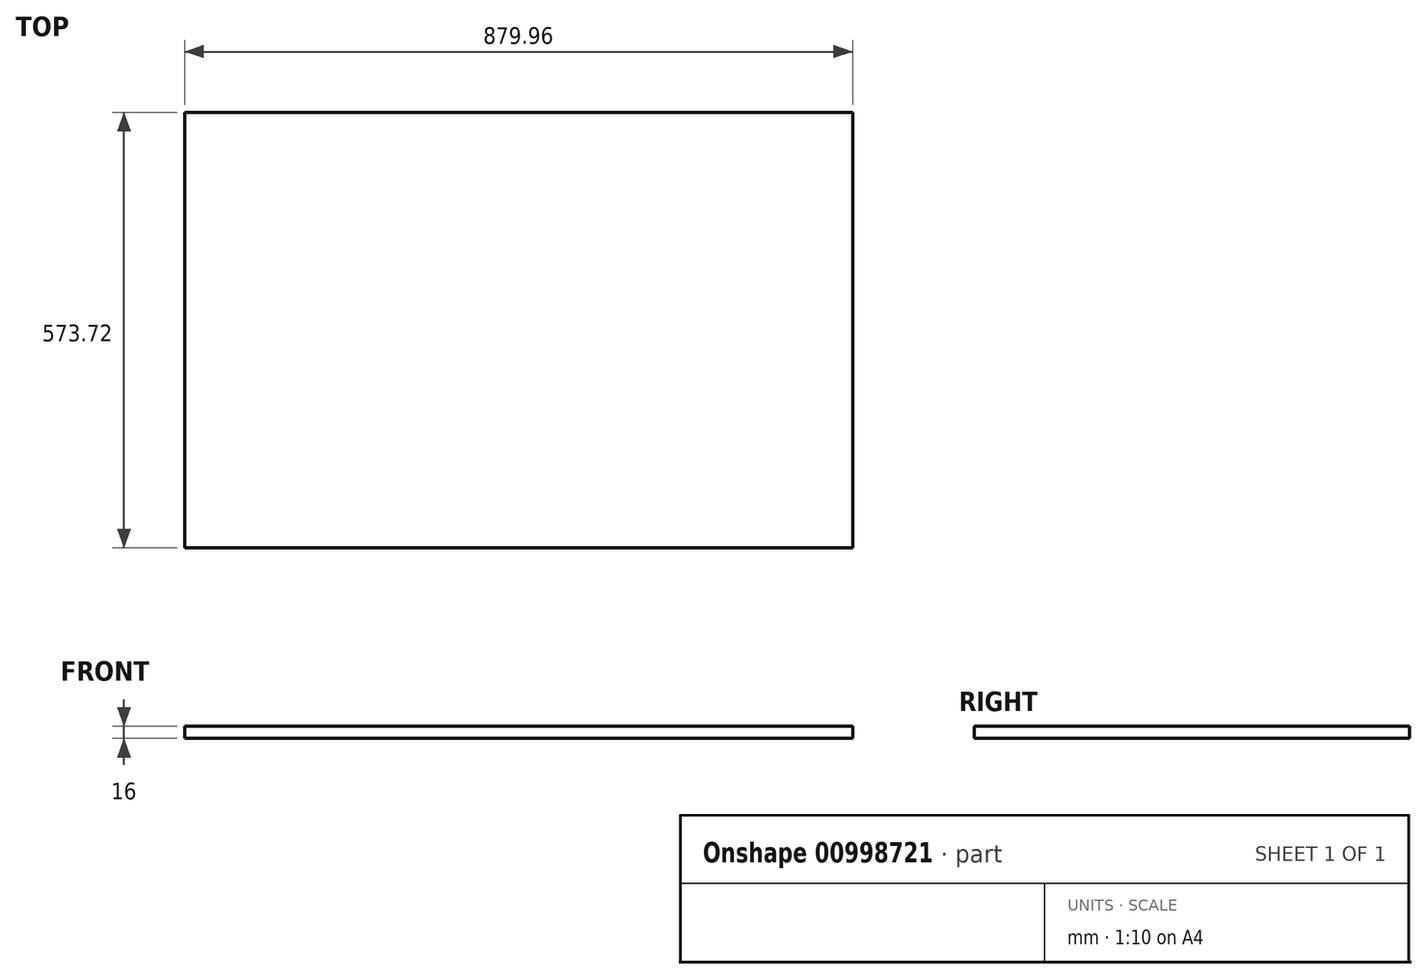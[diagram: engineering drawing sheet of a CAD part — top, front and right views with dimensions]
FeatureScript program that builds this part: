
annotation { "Feature Type Name" : "Feature", "Feature Type Description" : "" }
export const myFeature = defineFeature(function(context is Context, id is Id, definition is map)
    precondition{}
    {
        {
            var Q0;
            Q0=qCreatedBy(makeId("Top.planeOp"),FACE);
            var sketch = newSketch(context, id + "F0", { "sketchPlane" : qUnion([Q0])});
            skLineSegment(sketch, "E0.bottom", {"start": v(-50, -30) * mm, "end": v(950, -30) * mm});
            skLineSegment(sketch, "E0.top", {"start": v(-50, 570) * mm, "end": v(950, 570) * mm});
            skLineSegment(sketch, "E0.left", {"start": v(-50, -30) * mm, "end": v(-50, 570) * mm});
            skLineSegment(sketch, "E0.right", {"start": v(950, -30) * mm, "end": v(950, 570) * mm});
            skLineSegment(sketch, "E1", {"start": v(950, 570) * mm, "end": v(-50, 570) * mm});
            skSolve(sketch);
        }
        {
            var Q0;
            Q0=makeQuery(id+"F0.imprint","IMPRINT",FACE,{"disambiguationData":[TD([[makeQuery(id+"F0.imprint","IMPRINT",EDGE,{"derivedFrom":sQuery(id+"F0.wireOp",EDGE,"E0.left")}),-1.0]])]});
            extrude(context, id + "F1", {"entities" : qUnion([Q0]), "depth" : 380 * mm, "offsetDistance" : 25 * mm});
        }
        {
            var Q0;
            Q0=makeQuery(id+"F1.opExtrude","CAP_EDGE",EDGE,{"disambiguationData":[OSD([sQuery(id+"F0.wireOp",EDGE,"E0.left")])],"isStart":false});
            var Q1;
            Q1=makeQuery(id+"F1.opExtrude","CAP_EDGE",EDGE,{"disambiguationData":[OSD([sQuery(id+"F0.wireOp",EDGE,"E0.right")])],"isStart":false});
            fillet(context, id + "F2", {"entities" : qUnion([Q0, Q1]), "radius" : 60 * mm, "tangentPropagation" : true, "allowEdgeOverflow" : false});
        }
        {
            var Q0;
            Q0=makeQuery(id+"F1.opExtrude","CAP_EDGE",EDGE,{"disambiguationData":[OSD([sQuery(id+"F0.wireOp",EDGE,"E0.bottom")])],"isStart":true});
            var Q1;
            Q1=makeQuery(id+"F1.opExtrude","CAP_EDGE",EDGE,{"disambiguationData":[OSD([sQuery(id+"F0.wireOp",EDGE,"E1")])],"isStart":true});
            fillet(context, id + "F3", {"entities" : qUnion([Q0, Q1]), "radius" : 60 * mm, "tangentPropagation" : true, "allowEdgeOverflow" : false});
        }
        {
            var Q0;
            Q0=makeQuery(id+"F1.opExtrude","CAP_FACE",FACE,{"disambiguationData":[OSD([sQuery(id+"F0.wireOp",EDGE,"E0.left"),sQuery(id+"F0.wireOp",EDGE,"E0.right"),sQuery(id+"F0.wireOp",EDGE,"E0.bottom"),sQuery(id+"F0.wireOp",EDGE,"E1")])],"isStart":false});
            cPlane(context, id + "F4", {"entities" : qUnion([Q0]), "cplaneType" : CPlaneType.OFFSET, "offset" : 0 * mm, "width" : 150 * mm, "height" : 150 * mm});
        }
        {
            var Q0;
            Q0=makeQuery(id+"F1.opExtrude","CAP_EDGE",EDGE,{"disambiguationData":[OSD([sQuery(id+"F0.wireOp",EDGE,"E0.bottom")])],"isStart":false});
            cPoint(context, id + "F5", {"entities" : qUnion([Q0]), "parameter" : 0.5});
        }
        {
            var Q0;
            Q0 = qCreatedBy(id + "F5" ,VERTEX);
            var Q1;
            Q1=makeQuery(id+"F1.opExtrude","CAP_EDGE",EDGE,{"disambiguationData":[OSD([sQuery(id+"F0.wireOp",EDGE,"E0.bottom")])],"isStart":false});
            cPlane(context, id + "F6", {"entities" : qUnion([Q0, Q1]), "cplaneType" : CPlaneType.LINE_POINT, "offset" : 25 * mm, "width" : 150 * mm, "height" : 150 * mm});
        }
        {
            var Q0;
            Q0=qCreatedBy(id+"F6.planeOp",FACE);
            var sketch = newSketch(context, id + "F7", { "sketchPlane" : qUnion([Q0])});
            skCircle(sketch, "E2", {"center": v(-31.89, 381.57) * mm, "radius": 15 * mm});
            skSolve(sketch);
        }
        {
            var Q0;
            Q0=makeQuery(id+"F1.opExtrude","SWEPT_FACE",FACE,{"disambiguationData":[OSD([sQuery(id+"F0.wireOp",EDGE,"E0.bottom")])]});
            extrude(context, id + "F8", {"entities" : qUnion([Q0]), "operationType" : NewBodyOperationType.REMOVE, "endBound" : BoundingType.THROUGH_ALL, "oppositeDirection" : true, "depth" : 25 * mm, "offsetDistance" : 25 * mm});
        }
        {
            var Q0;
            Q0=makeQuery(id+"F1.opExtrude","SWEPT_FACE",FACE,{"disambiguationData":[OSD([sQuery(id+"F0.wireOp",EDGE,"E0.right")])]});
            extrude(context, id + "F9", {"entities" : qUnion([Q0]), "operationType" : NewBodyOperationType.REMOVE, "endBound" : BoundingType.THROUGH_ALL, "oppositeDirection" : true, "depth" : 25 * mm, "offsetDistance" : 25 * mm});
        }
        {
            var Q0;
            Q0=qCreatedBy(id+"F4.planeOp",FACE);
            var sketch = newSketch(context, id + "F10", { "sketchPlane" : qUnion([Q0])});
            skLineSegment(sketch, "E3.bottom", {"start": v(889.96, 556.82) * mm, "end": v(10, 556.82) * mm});
            skLineSegment(sketch, "E3.top", {"start": v(889.96, -16.9) * mm, "end": v(10, -16.9) * mm});
            skLineSegment(sketch, "E3.left", {"start": v(889.96, 556.82) * mm, "end": v(889.96, -16.9) * mm});
            skLineSegment(sketch, "E3.right", {"start": v(10, 556.82) * mm, "end": v(10, -16.9) * mm});
            skSolve(sketch);
        }
        {
            var Q0;
            Q0=makeQuery(id+"F10.imprint","IMPRINT",FACE,{"disambiguationData":[TD([[makeQuery(id+"F10.imprint","IMPRINT",EDGE,{"derivedFrom":sQuery(id+"F10.wireOp",EDGE,"E3.bottom")}),1.0]])]});
            extrude(context, id + "F11", {"entities" : qUnion([Q0]), "oppositeDirection" : true, "depth" : 6 * mm, "offsetDistance" : 25 * mm});
        }
        {
            var Q0;
            Q0=makeQuery(id+"F11.opExtrude","CAP_FACE",FACE,{"disambiguationData":[OSD([sQuery(id+"F10.wireOp",EDGE,"E3.bottom"),sQuery(id+"F10.wireOp",EDGE,"E3.top"),sQuery(id+"F10.wireOp",EDGE,"E3.left"),sQuery(id+"F10.wireOp",EDGE,"E3.right")])],"isStart":true});
            extrude(context, id + "F12", {"entities" : qUnion([Q0]), "operationType" : NewBodyOperationType.ADD, "depth" : 10 * mm, "offsetDistance" : 25 * mm});
        }
    });
